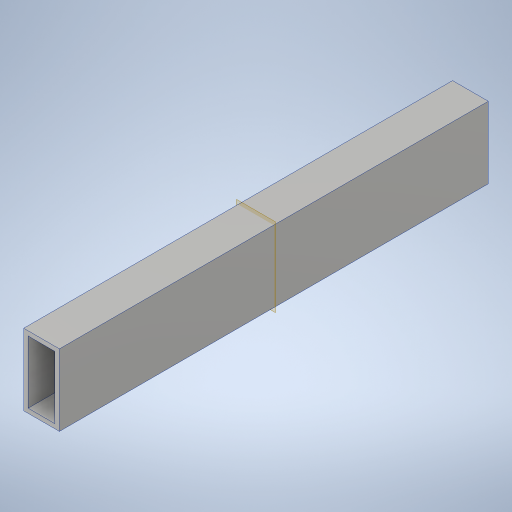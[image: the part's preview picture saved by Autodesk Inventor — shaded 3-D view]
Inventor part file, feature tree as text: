
AUTODESK INVENTOR PART (.ipt)
format: ipt  version: 2023.4 (Build 274418000, 418)  size: 228,864 bytes
history: native  units: in
note: dims shown in document units (in); Inventor stores cm internally (conversion verified against a paired STEP export)
features: extrude x1
ambient origin geometry x8: Origin, YZ Plane, XZ Plane, XY Plane, X Axis, Y Axis, Z Axis, Center Point
bodies: Solid1 (feature_tree)
feature tree (1):
  extrude  "Extrusion1"  TaperAngle=0.0deg  [1 undecoded]
note: 1 required parameter value undecoded (feature->parameter linkage not recoverable at this tier; creation-order binding heuristic only, values carry confidence <= 0.55)
